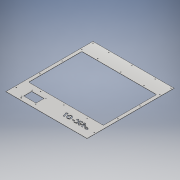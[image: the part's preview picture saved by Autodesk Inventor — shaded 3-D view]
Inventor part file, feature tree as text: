
AUTODESK INVENTOR PART (.ipt)
format: ipt  version: 2019 (Build 230136000, 136)  size: 630,272 bytes
history: native  units: mm
features: sketch x6, other x5, sheet_metal_op x3, fillet x1, hole x1, extrude x1
ambient origin geometry x8: Origin, YZ Plane, XZ Plane, XY Plane, X Axis, Y Axis, Z Axis, Center Point
bodies: Body1 (feature_tree)
feature tree (17):
  sheet_metal_op  "Face4"
  fillet  "Fillet1"  Radius=513.0mm
  hole  "Hole1"  [1 undecoded]
  extrude  "Extrusion1"  Depth=10.0mm
  sheet_metal_op  "Face5"
  sketch  "Sketch1"  dims[d1=550.0mm d2=10.0mm]
  other  "Plate4"
  sketch  "Sketch2"  dims[d3=10.0mm d4=10.0mm]
  sketch  "Sketch3"  dims[d5=110.0mm]
  sketch  "Sketch4"  dims[d6=80.0mm]
  sketch  "Sketch5"  dims[d7=110.0mm]
  sketch  "Sketch6"  dims[d8=110.0mm d9=70.0mm d10=55.0mm d11=4.2mm d12=0.8mm d13=0.8mm d14=10.0mm d15=10.0mm d16=0.8mm d17=13.0mm d18=10.0mm d19=0.8mm d20=5.0mm d21=1.5mm d22=78.45mm d23=51.0mm d25=40.0mm d26=1.5mm d27=0.0mm d28=80.0mm d29=6.5mm d30=18.3mm d31=3.05mm d32=1.5mm d33=0.0mm d34=87.95mm d35=65.0mm d36=3.4mm d37=3.4mm d38=6.0mm d39=4.0mm d40=2.0mm d41=90.0deg d42=1.5mm d43=20.594885mm d44=61.5mm d46=128.25mm d47=10.0mm d48=0.0mm d49=2.0mm d51=2.0mm d52=37.821388mm d53=0.8mm d54=0.2mm d55=0.2mm d56=0.2mm d57=0.8mm]
  other  "Plate5"
  sheet_metal_op  "Bend1"
  other  "Cut1"
  other  "Cut2"
  other  "Definition1"
note: 1 required parameter value undecoded (feature->parameter linkage not recoverable at this tier; creation-order binding heuristic only, values carry confidence <= 0.55)
